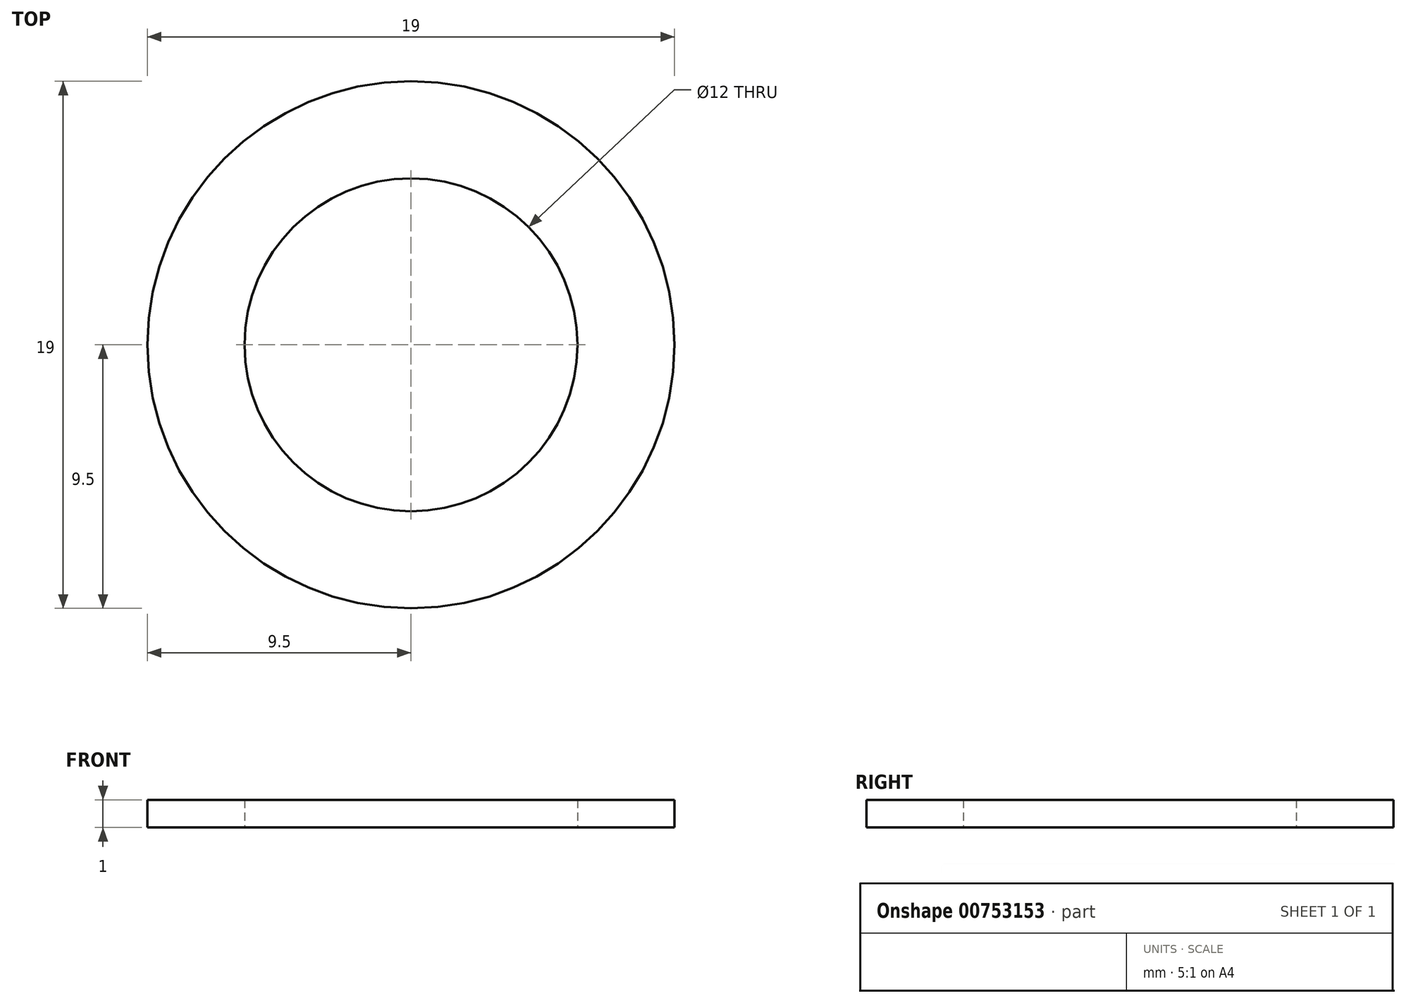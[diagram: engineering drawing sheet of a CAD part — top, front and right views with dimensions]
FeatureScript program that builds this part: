
annotation { "Feature Type Name" : "Feature", "Feature Type Description" : "" }
export const myFeature = defineFeature(function(context is Context, id is Id, definition is map)
    precondition{}
    {
        {
            var Q0;
            Q0=qCreatedBy(makeId("Top.planeOp"),FACE);
            var sketch = newSketch(context, id + "F0", { "sketchPlane" : qUnion([Q0])});
            skCircle(sketch, "E0", {"center": v(0, 0) * mm, "radius": 9.5 * mm});
            skCircle(sketch, "E1", {"center": v(0, 0) * mm, "radius": 6 * mm});
            skSolve(sketch);
        }
        {
            var Q0;
            Q0 = qSketchRegion(id + "F0", true);
            extrude(context, id + "F1", {"entities" : qUnion([Q0]), "depth" : 1 * mm, "offsetDistance" : 25 * mm});
        }
    });
